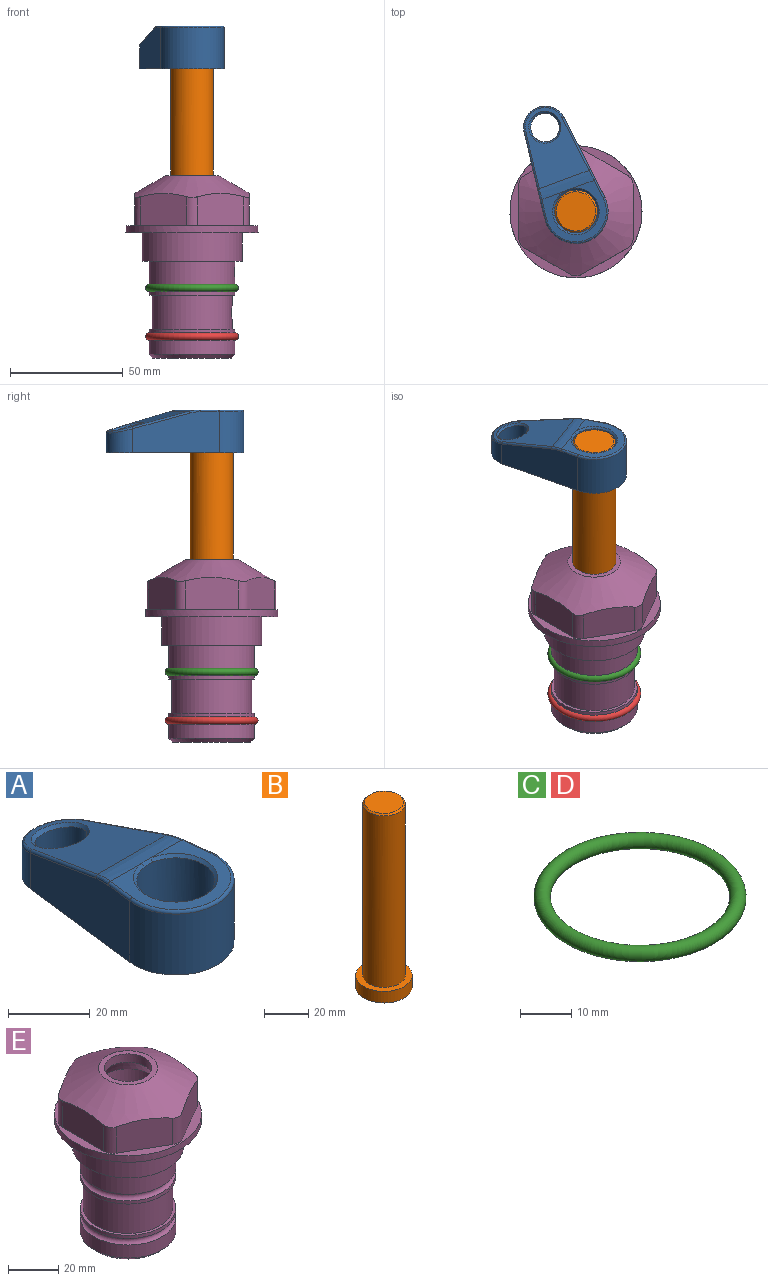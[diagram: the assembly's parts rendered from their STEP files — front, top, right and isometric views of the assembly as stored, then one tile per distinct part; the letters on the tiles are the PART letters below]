
ASSEMBLY  parts=5 mates=4
PART A: 31 faces, bbox 31.7x65.5x19.8 mm
  f0: plane 39.12x18.26mm, normal (0.99,0.12,0), area 612.2mm2, adj f1,f4,f7,f11,f13,f15
  f1: cylinder r=9.53mm len=18.91mm, axis (0,0,-1), area 296.1mm2, adj f0,f2,f7,f17
  f2: plane 39.12x18.26mm, normal (-0.99,0.12,0), area 612.2mm2, adj f1,f4,f7,f12,f14,f16
  f3: cylinder r=6.35mm len=12.7mm, axis (0,0,-1), area 362.4mm2, adj f7,f18
  f4: cylinder r=14.29mm len=28.58mm, axis (0,0,-1), area 882.2mm2, adj f0,f2,f7,f10
  f5: cylinder r=9.53mm len=19.05mm, axis (0,0,-1), area 1092.6mm2, adj f7,f19,f20
  f6: plane 26.99x23.69mm, normal (0,0,1), area 216.2mm2, adj f9,f10,f11,f12,f19
  f7: plane 63.5x28.58mm, normal (0,0,-1), area 661.8mm2, adj f0,f1,f2,f3,f4,f5,f22,f23
  f8: plane 33.52x23.6mm, normal (0,0.26,0.97), area 486mm2, adj f9,f15,f16,f17,f18
  f9: cylinder r=19.05mm len=24.72mm, axis (1,0,0), area 120.4mm2, adj f6,f8,f13,f14,f20
  f10: torus R=13.49mm, axis (0,0,1), area 59mm2, adj f4,f6,f11,f12
  f11: cylinder r=0.79mm len=8.67mm, axis (0.12,-0.99,0), area 10.8mm2, adj f0,f6,f10,f13
  f12: cylinder r=0.79mm len=8.67mm, axis (0.12,0.99,0), area 10.8mm2, adj f2,f6,f10,f14
  f13: bspline ~4.95x1.42mm, area 6.1mm2, adj f0,f9,f11,f15
  f14: bspline ~4.95x1.42mm, area 6.1mm2, adj f2,f9,f12,f16
  f15: cylinder r=0.79mm len=25.95mm, axis (0.12,-0.96,0.26), area 32.9mm2, adj f0,f8,f13,f17
  f16: cylinder r=0.79mm len=25.95mm, axis (0.12,0.96,-0.26), area 32.9mm2, adj f2,f8,f14,f17
  f17: bspline ~18.91x8.38mm, area 30mm2, adj f1,f8,f15,f16
  f18: bspline ~14.29x14.29mm, area 48.3mm2, adj f3,f8
  f19: cone r=9.53mm half-angle=45deg, axis (0,0,1), area 66.5mm2, adj f5,f6,f20
  f20: bspline ~3.22x0.96mm, area 3.5mm2, adj f5,f9,f19
  f21: plane 2.75x2.72mm, normal (0,0,-1), area 2.9mm2, adj f23,f25,f28
  f22: plane 23.05x15.88mm, normal (-0.99,-0.12,0), area 323.6mm2, adj f7,f25,f26,f27,f28,f29
  f23: plane 23.05x15.88mm, normal (0.99,-0.12,0), area 323.6mm2, adj f7,f21,f25,f27,f28,f30
  f24: cylinder r=9.53mm len=10.69mm, axis (0,0,-1), area 114.7mm2, adj f7,f27,f29,f30
  f25: cylinder r=12.7mm len=20.59mm, axis (0,0,-1), area 381.1mm2, adj f7,f21,f22,f23,f26,f28
  f26: plane 2.75x2.72mm, normal (0,0,-1), area 2.9mm2, adj f22,f25,f28
  f27: plane 19.72x18.37mm, normal (0,-0.26,-0.97), area 291.8mm2, adj f22,f23,f24,f28,f29,f30
  f28: cylinder r=15.88mm len=19.92mm, axis (1,0,0), area 54.8mm2, adj f21,f22,f23,f25,f26,f27
  f29: cylinder r=1.59mm len=11mm, axis (0,0,-1), area 34.7mm2, adj f7,f22,f24,f27
  f30: cylinder r=1.59mm len=11mm, axis (0,0,-1), area 34.7mm2, adj f7,f23,f24,f27
PART B: 6 faces, bbox 25.4x25.4x101.6 mm
  f0: plane 17.46x17.46mm, normal (0,0,1), area 239.5mm2, adj f5
  f1: plane 25.4x25.4mm, normal (0,0,-1), area 506.7mm2, adj f2
  f2: cylinder r=12.7mm len=25.4mm, axis (0,0,1), area 506.7mm2, adj f1,f3
  f3: plane 25.4x25.4mm, normal (0,0,1), area 221.7mm2, adj f2,f4
  f4: cylinder r=9.53mm len=94.46mm, axis (0,0,1), area 5653mm2, adj f3,f5
  f5: cone r=8.73mm half-angle=45deg, axis (0,0,-1), area 64.4mm2, adj f0,f4
PART C: 1 faces, bbox 44.7x44.7x3.2 mm
  f0: torus R=19.05mm, axis (0,0,1), area 1193.9mm2
PART D: same geometry as C
PART E: 36 faces, bbox 58.7x58.7x81 mm
  f0: cylinder r=17.78mm len=35.56mm, axis (0,0,1), area 1670.8mm2, adj f23,f24,f31
  f1: cylinder r=19.05mm len=38.1mm, axis (0,0,1), area 1191.9mm2, adj f26,f27,f30
  f2: plane 58.66x58.66mm, normal (0,0,-1), area 1150.6mm2, adj f3,f28
  f3: cylinder r=29.33mm len=58.66mm, axis (0,0,-1), area 585.1mm2, adj f2,f4
  f4: plane 58.66x58.66mm, normal (0,0,1), area 475.9mm2, adj f3,f5,f6,f7,f8,f9,f10,f11
  f5: plane 20.32x14.34mm, normal (-0.5,0.87,0), area 324.4mm2, adj f4,f15,f16,f17
  f6: plane 20.32x14.34mm, normal (0.5,0.87,0), area 324.4mm2, adj f4,f14,f15,f17
  f7: plane 23.48x14.34mm, normal (1,0,0), area 324.4mm2, adj f4,f13,f14,f17
  f8: plane 20.32x14.34mm, normal (0.5,-0.87,0), area 324.4mm2, adj f4,f12,f13,f17
  f9: plane 20.32x14.34mm, normal (-0.5,-0.87,0), area 324.4mm2, adj f4,f11,f12,f17
  f10: plane 23.48x14.34mm, normal (-1,0,0), area 324.4mm2, adj f4,f11,f16,f17
  f11: cylinder r=5.08mm len=12.85mm, axis (0,0,-1), area 67.2mm2, adj f4,f9,f10,f17
  f12: cylinder r=5.08mm len=12.85mm, axis (0,0,-1), area 67.2mm2, adj f4,f8,f9,f17
  f13: cylinder r=5.08mm len=12.85mm, axis (0,0,-1), area 67.2mm2, adj f4,f7,f8,f17
  f14: cylinder r=5.08mm len=12.85mm, axis (0,0,-1), area 67.2mm2, adj f4,f6,f7,f17
  f15: cylinder r=5.08mm len=12.85mm, axis (0,0,-1), area 67.2mm2, adj f4,f5,f6,f17
  f16: cylinder r=5.08mm len=12.85mm, axis (0,0,-1), area 67.2mm2, adj f4,f5,f10,f17
  f17: cone r=11.73mm half-angle=60deg, axis (0,0,-1), area 2071.8mm2, adj f5,f6,f7,f8,f9,f10,f11,f12
  f18: plane 23.46x23.46mm, normal (0,0,1), area 147.4mm2, adj f17,f35
  f19: plane 34.93x34.93mm, normal (0,0,-1), area 958mm2, adj f29
  f20: cylinder r=19.05mm len=38.1mm, axis (0,0,1), area 760.1mm2, adj f21,f29
  f21: torus R=19.05mm, axis (0,0,1), area 565.3mm2, adj f20,f22
  f22: cylinder r=19.05mm len=38.1mm, axis (0,0,1), area 190mm2, adj f21,f23
  f23: plane 38.1x38.1mm, normal (0,0,1), area 146.9mm2, adj f0,f22
  f24: plane 38.1x38.1mm, normal (0,0,-1), area 146.9mm2, adj f0,f25
  f25: cylinder r=19.05mm len=38.1mm, axis (0,0,1), area 190mm2, adj f24,f26
  f26: torus R=19.05mm, axis (0,0,1), area 565.3mm2, adj f1,f25
  f27: plane 44.45x44.45mm, normal (0,0,-1), area 411.7mm2, adj f1,f28
  f28: cylinder r=22.23mm len=44.45mm, axis (0,0,1), area 1773.5mm2, adj f2,f27
  f29: cone r=19.05mm half-angle=45deg, axis (0,0,1), area 257.5mm2, adj f19,f20
  f30: cylinder r=3.17mm len=6.75mm, axis (-1,0,0), area 128mm2, adj f1,f33
  f31: cylinder r=3.17mm len=6.35mm, axis (-1,0,0), area 102.5mm2, adj f0,f33
  f32: plane 25.4x25.4mm, normal (0,0,1), area 506.7mm2, adj f33
  f33: cylinder r=12.7mm len=66.42mm, axis (0,0,-1), area 5236.2mm2, adj f30,f31,f32,f34
  f34: cone r=9.53mm half-angle=30deg, axis (0,0,-1), area 443.4mm2, adj f33,f35
  f35: cylinder r=9.53mm len=19.05mm, axis (0,0,-1), area 240.9mm2, adj f18,f34
PLACE A rot(axis=(0,0,1),20.3deg) t=(0,0,28.35)mm
PLACE B rot(axis=(0,0,1),20.3deg) t=(0,0,27.55)mm
PLACE C at identity
PLACE D t=(0,0,-21.59)mm
PLACE E at identity fixed
MATE cylindrical E.f0 <-> B.f2  axis (0,0,1) through (0,0,-50.55)mm
MATE fastened D.f0 <-> E.f0  axis (0,0,1) through (0,0,-46.1)mm
MATE fastened C.f0 <-> E.f0  axis (0,0,1) through (0,0,-24.51)mm
MATE fastened A.f4 <-> B.f2  axis (0,0,-1) through (0,0,91.05)mm
